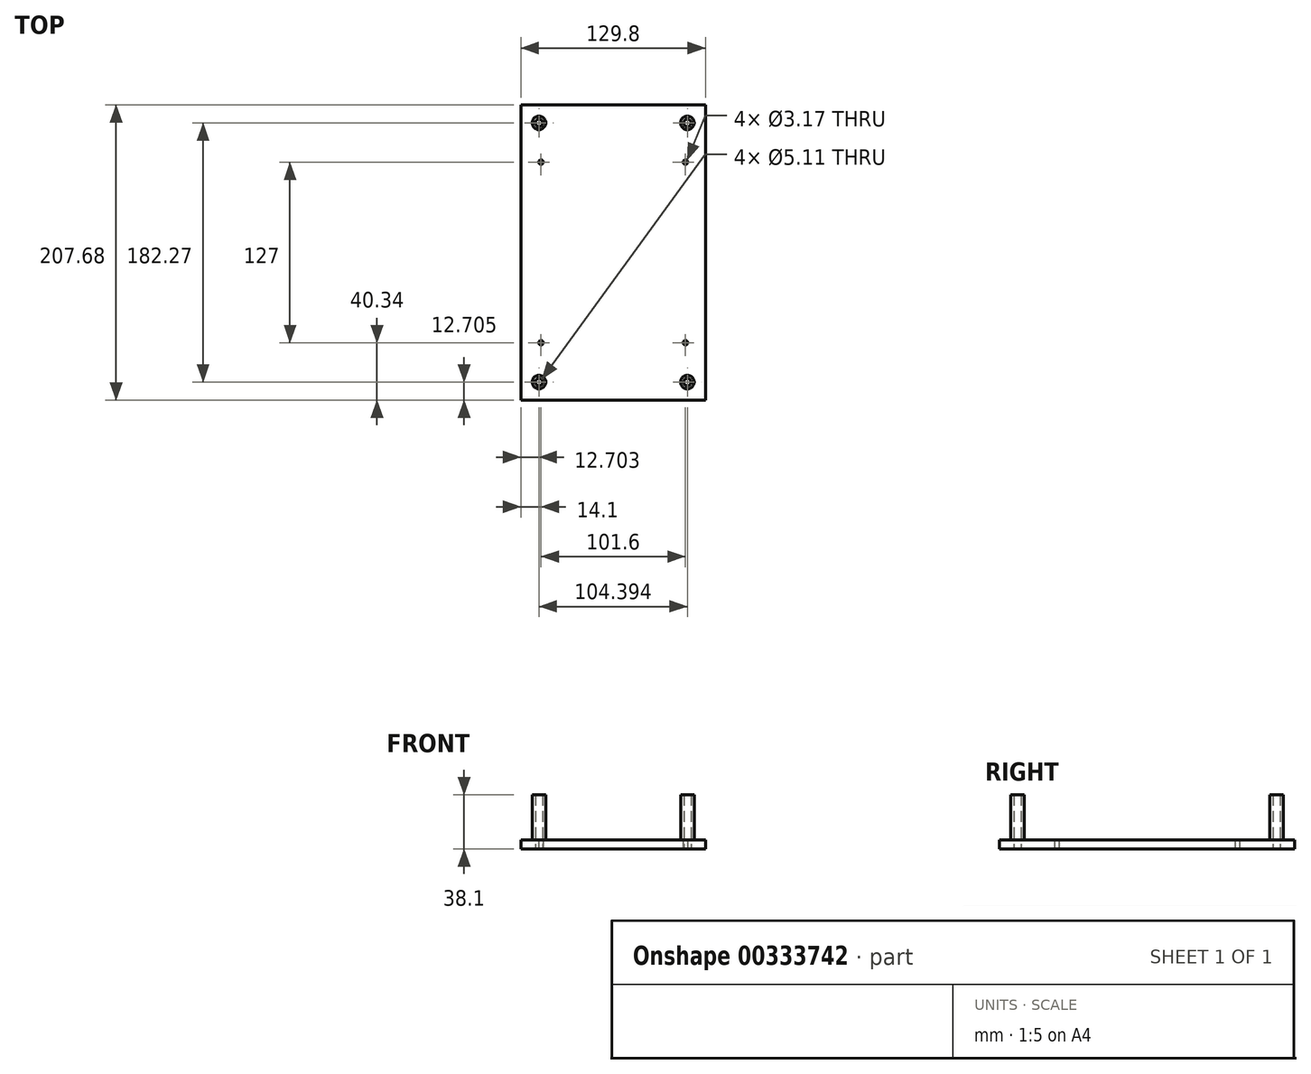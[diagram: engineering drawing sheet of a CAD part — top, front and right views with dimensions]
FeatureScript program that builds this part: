
annotation { "Feature Type Name" : "Feature", "Feature Type Description" : "" }
export const myFeature = defineFeature(function(context is Context, id is Id, definition is map)
    precondition{}
    {
        {
            var Q0;
            Q0=qCreatedBy(makeId("Top.planeOp"),FACE);
            var sketch = newSketch(context, id + "F0", { "sketchPlane" : qUnion([Q0])});
            skLineSegment(sketch, "E0.bottom", {"start": v(64.9, 103.84) * mm, "end": v(-64.9, 103.84) * mm});
            skLineSegment(sketch, "E0.top", {"start": v(64.9, -103.84) * mm, "end": v(-64.9, -103.84) * mm});
            skLineSegment(sketch, "E0.left", {"start": v(64.9, 103.84) * mm, "end": v(64.9, -103.84) * mm});
            skLineSegment(sketch, "E0.right", {"start": v(-64.9, 103.84) * mm, "end": v(-64.9, -103.84) * mm});
            skPoint(sketch, "E0.middle", {"position": v(0, 0) * mm});
            skLineSegment(sketch, "E1.bottom", {"start": v(52.2, 91.14) * mm, "end": v(-52.2, 91.14) * mm, "construction": true});
            skLineSegment(sketch, "E1.top", {"start": v(52.2, -91.14) * mm, "end": v(-52.2, -91.14) * mm, "construction": true});
            skLineSegment(sketch, "E1.left", {"start": v(52.2, 91.14) * mm, "end": v(52.2, -91.14) * mm, "construction": true});
            skLineSegment(sketch, "E1.right", {"start": v(-52.2, 91.14) * mm, "end": v(-52.2, -91.14) * mm, "construction": true});
            skCircle(sketch, "E2", {"center": v(52.2, 91.14) * mm, "radius": 2.55 * mm});
            skCircle(sketch, "E3", {"center": v(-52.2, 91.14) * mm, "radius": 2.55 * mm});
            skCircle(sketch, "E4", {"center": v(-52.2, -91.14) * mm, "radius": 2.55 * mm});
            skCircle(sketch, "E5", {"center": v(52.2, -91.14) * mm, "radius": 2.55 * mm});
            skLineSegment(sketch, "E6.bottom", {"start": v(50.8, 63.5) * mm, "end": v(-50.8, 63.5) * mm, "construction": true});
            skLineSegment(sketch, "E6.top", {"start": v(50.8, -63.5) * mm, "end": v(-50.8, -63.5) * mm, "construction": true});
            skLineSegment(sketch, "E6.left", {"start": v(50.8, 63.5) * mm, "end": v(50.8, -63.5) * mm, "construction": true});
            skLineSegment(sketch, "E6.right", {"start": v(-50.8, 63.5) * mm, "end": v(-50.8, -63.5) * mm, "construction": true});
            skLineSegment(sketch, "E7.bottom", {"start": v(73, 73) * mm, "end": v(-73, 73) * mm, "construction": true});
            skLineSegment(sketch, "E7.top", {"start": v(73, -73) * mm, "end": v(-73, -73) * mm, "construction": true});
            skLineSegment(sketch, "E7.left", {"start": v(73, 73) * mm, "end": v(73, -73) * mm, "construction": true});
            skLineSegment(sketch, "E7.right", {"start": v(-73, 73) * mm, "end": v(-73, -73) * mm, "construction": true});
            skCircle(sketch, "E8", {"center": v(-50.8, 63.5) * mm, "radius": 1.59 * mm});
            skCircle(sketch, "E9", {"center": v(50.8, 63.5) * mm, "radius": 1.59 * mm});
            skCircle(sketch, "E10", {"center": v(50.8, -63.5) * mm, "radius": 1.59 * mm});
            skCircle(sketch, "E11", {"center": v(-50.8, -63.5) * mm, "radius": 1.59 * mm});
            skSolve(sketch);
        }
        {
            var Q0;
            Q0=makeQuery(id+"F0.imprint","IMPRINT",FACE,{"disambiguationData":[TD([[makeQuery(id+"F0.imprint","IMPRINT",EDGE,{"derivedFrom":sQuery(id+"F0.wireOp",EDGE,"E0.bottom")}),1.0]])]});
            extrude(context, id + "F1", {"entities" : qUnion([Q0]), "depth" : 6.35 * mm});
        }
        {
            var Q0;
            Q0=makeQuery(id+"F1.opExtrude","CAP_FACE",FACE,{"disambiguationData":[OSD([sQuery(id+"F0.wireOp",EDGE,"E0.bottom"),sQuery(id+"F0.wireOp",EDGE,"E0.top"),sQuery(id+"F0.wireOp",EDGE,"E0.left"),sQuery(id+"F0.wireOp",EDGE,"E0.right"),sQuery(id+"F0.wireOp",EDGE,"E2"),sQuery(id+"F0.wireOp",EDGE,"E3"),sQuery(id+"F0.wireOp",EDGE,"E4"),sQuery(id+"F0.wireOp",EDGE,"E5"),sQuery(id+"F0.wireOp",EDGE,"E8"),sQuery(id+"F0.wireOp",EDGE,"E9"),sQuery(id+"F0.wireOp",EDGE,"E10"),sQuery(id+"F0.wireOp",EDGE,"E11")])],"isStart":false});
            var sketch = newSketch(context, id + "F2", { "sketchPlane" : qUnion([Q0])});
            skCircle(sketch, "E12", {"center": v(52.2, 91.14) * mm, "radius": 4.76 * mm});
            skCircle(sketch, "E13", {"center": v(-52.2, 91.14) * mm, "radius": 4.76 * mm});
            skCircle(sketch, "E14", {"center": v(-52.2, -91.14) * mm, "radius": 4.76 * mm});
            skCircle(sketch, "E15", {"center": v(52.2, -91.14) * mm, "radius": 4.76 * mm});
            skCircle(sketch, "E16", {"center": v(52.2, 91.14) * mm, "radius": 2.55 * mm});
            skCircle(sketch, "E17", {"center": v(-52.2, 91.14) * mm, "radius": 2.55 * mm});
            skCircle(sketch, "E18", {"center": v(-52.2, -91.14) * mm, "radius": 2.55 * mm});
            skCircle(sketch, "E19", {"center": v(52.2, -91.14) * mm, "radius": 2.55 * mm});
            skSolve(sketch);
        }
        {
            var Q0;
            Q0=makeQuery(id+"F2.imprint","IMPRINT",FACE,{"disambiguationData":[TD([[makeQuery(id+"F2.imprint","IMPRINT",EDGE,{"derivedFrom":sQuery(id+"F2.wireOp",EDGE,"E13")}),1.0]])]});
            var Q1;
            Q1=makeQuery(id+"F2.imprint","IMPRINT",FACE,{"disambiguationData":[TD([[makeQuery(id+"F2.imprint","IMPRINT",EDGE,{"derivedFrom":sQuery(id+"F2.wireOp",EDGE,"E12")}),1.0]])]});
            var Q2;
            Q2=makeQuery(id+"F2.imprint","IMPRINT",FACE,{"disambiguationData":[TD([[makeQuery(id+"F2.imprint","IMPRINT",EDGE,{"derivedFrom":sQuery(id+"F2.wireOp",EDGE,"E15")}),1.0]])]});
            var Q3;
            Q3=makeQuery(id+"F2.imprint","IMPRINT",FACE,{"disambiguationData":[TD([[makeQuery(id+"F2.imprint","IMPRINT",EDGE,{"derivedFrom":sQuery(id+"F2.wireOp",EDGE,"E14")}),1.0]])]});
            extrude(context, id + "F3", {"entities" : qUnion([Q0, Q1, Q2, Q3]), "operationType" : NewBodyOperationType.ADD, "depth" : 31.75 * mm});
        }
    });
